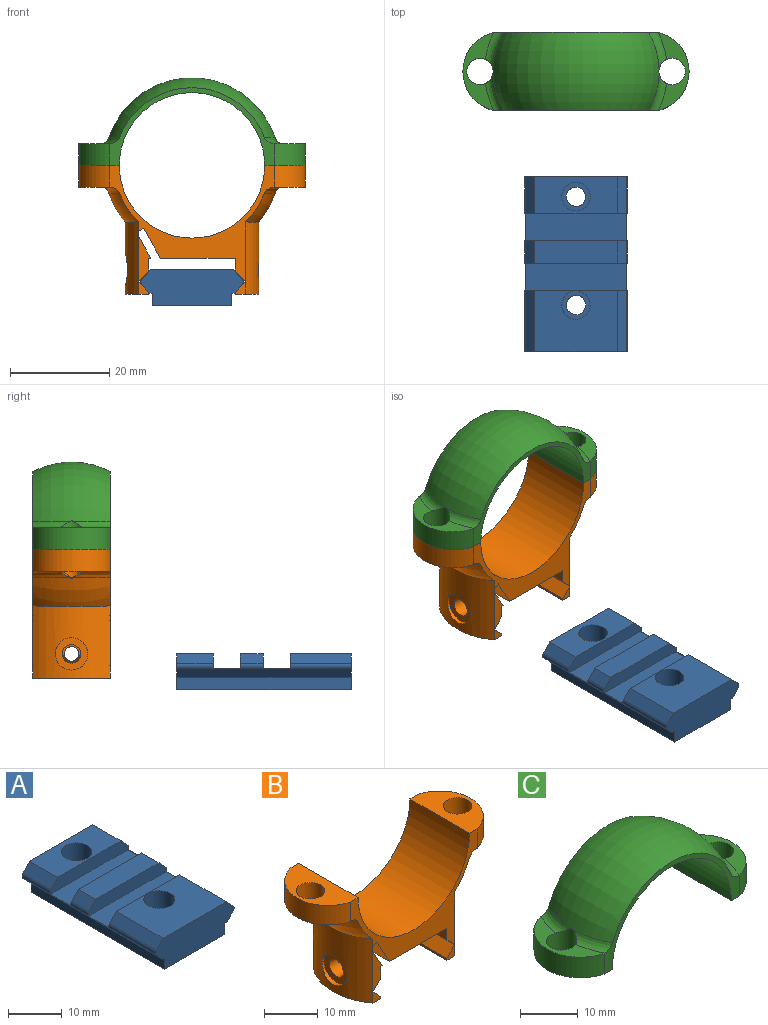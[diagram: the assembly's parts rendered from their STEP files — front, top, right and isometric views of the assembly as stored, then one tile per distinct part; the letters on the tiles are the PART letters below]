
ASSEMBLY  parts=3 mates=2
PART A: 32 faces, bbox 20.7x35.1x7.3 mm
  f0: cylinder r=0.75mm len=35.14mm, axis (0,1,0), area 28.3mm2, adj f1,f2,f14,f15,f18,f19,f20,f21
  f1: plane 4.57x1.92mm, normal (0.73,0,0.69), area 12.1mm2, adj f0,f3,f22,f24
  f2: plane 7.4x1.92mm, normal (0.73,0,0.69), area 19.6mm2, adj f0,f4,f19,f25
  f3: plane 16.66x4.57mm, normal (0,0,1), area 76.1mm2, adj f1,f5,f22,f24
  f4: plane 16.66x7.4mm, normal (0,0,1), area 97.3mm2, adj f2,f6,f19,f25,f31
  f5: plane 4.57x1.92mm, normal (-0.73,0,0.69), area 12.1mm2, adj f3,f7,f22,f24
  f6: plane 7.4x1.92mm, normal (-0.73,0,0.69), area 19.6mm2, adj f4,f7,f19,f25
  f7: cylinder r=0.75mm len=35.14mm, axis (0,1,0), area 28.3mm2, adj f5,f6,f8,f17,f18,f19,f20,f21
  f8: plane 35.14x1.8mm, normal (-0.73,0,-0.69), area 87mm2, adj f7,f9,f18,f19
  f9: plane 35.14x0.49mm, normal (0,0,-1), area 17.3mm2, adj f8,f10,f18,f19
  f10: plane 35.14x2.5mm, normal (-1,0,0), area 87.9mm2, adj f9,f11,f18,f19
  f11: plane 35.14x15.91mm, normal (0,0,-1), area 535.4mm2, adj f10,f12,f18,f19,f26,f29
  f12: plane 35.14x2.5mm, normal (1,0,0), area 87.9mm2, adj f11,f13,f18,f19
  f13: plane 35.14x0.49mm, normal (0,0,-1), area 17.3mm2, adj f12,f14,f18,f19
  f14: plane 35.14x1.8mm, normal (0.73,0,-0.69), area 87mm2, adj f0,f13,f18,f19
  f15: plane 12.29x1.92mm, normal (0.73,0,0.69), area 32.5mm2, adj f0,f16,f18,f21
  f16: plane 16.66x12.29mm, normal (0,0,1), area 178.8mm2, adj f15,f17,f18,f21,f28
  f17: plane 12.29x1.92mm, normal (-0.73,0,0.69), area 32.5mm2, adj f7,f16,f18,f21
  f18: plane 20.7x7.25mm, normal (0,-1,0), area 129.9mm2, adj f0,f7,f8,f9,f10,f11,f12,f13
  f19: plane 20.7x7.25mm, normal (0,1,0), area 129.9mm2, adj f0,f2,f4,f6,f7,f8,f9,f10
  f20: plane 20.38x5.44mm, normal (0,0,1), area 110.9mm2, adj f0,f7,f21,f22
  f21: plane 20.7x2.9mm, normal (0,1,0), area 55.6mm2, adj f0,f7,f15,f16,f17,f20
  f22: plane 20.7x2.9mm, normal (0,-1,0), area 55.6mm2, adj f0,f1,f3,f5,f7,f20
  f23: plane 20.38x5.44mm, normal (0,0,1), area 110.9mm2, adj f0,f7,f24,f25
  f24: plane 20.7x2.9mm, normal (0,1,0), area 55.6mm2, adj f0,f1,f3,f5,f7,f23
  f25: plane 20.7x2.9mm, normal (0,-1,0), area 55.6mm2, adj f0,f2,f4,f6,f7,f23
  f26: cylinder r=1.94mm len=3.88mm, axis (0,0,1), area 37.2mm2, adj f11,f27
  f27: plane 5.75x5.75mm, normal (0,0,1), area 14.1mm2, adj f26,f28
  f28: cylinder r=2.88mm len=5.75mm, axis (0,0,1), area 75.9mm2, adj f16,f27
  f29: cylinder r=1.94mm len=3.88mm, axis (0,0,1), area 37.2mm2, adj f11,f30
  f30: plane 5.75x5.75mm, normal (0,0,1), area 14.1mm2, adj f29,f31
  f31: cylinder r=2.88mm len=5.75mm, axis (0,0,1), area 75.9mm2, adj f4,f30
PART B: 53 faces, bbox 46.4x20.6x26.1 mm
  f0: cylinder r=12.78mm len=15.65mm, axis (0,0,-1), area 238.4mm2, adj f3,f5,f7,f11,f22,f29,f44
  f1: cylinder r=12.78mm len=15.65mm, axis (0,0,-1), area 211.7mm2, adj f2,f3,f5,f6,f8,f9,f12,f30
  f2: plane 9.08x2.44mm, normal (0,-1,0), area 12.6mm2, adj f1,f15,f16,f17,f37
  f3: plane 33.42x23.55mm, normal (0,1,0), area 144.3mm2, adj f0,f1,f4,f10,f18,f19,f24,f25
  f4: plane 15.65x15.08mm, normal (0,0,-1), area 235.9mm2, adj f3,f5,f18,f38
  f5: plane 33.42x23.55mm, normal (0,-1,0), area 144.3mm2, adj f0,f1,f4,f10,f18,f19,f24,f25
  f6: plane 2.55x2mm, normal (0,-1,0), area 3mm2, adj f1,f12,f13,f14
  f7: plane 2.55x2mm, normal (0,1,0), area 3mm2, adj f0,f20,f21,f22
  f8: plane 9.08x2.44mm, normal (0,1,0), area 12.6mm2, adj f1,f15,f16,f17,f37
  f9: plane 2.55x2mm, normal (0,1,0), area 3mm2, adj f1,f12,f13,f14
  f10: cylinder r=14.62mm len=29.25mm, axis (0,1,0), area 719.1mm2, adj f3,f5,f26,f32
  f11: plane 2.55x2mm, normal (0,-1,0), area 3mm2, adj f0,f20,f21,f22
  f12: plane 15.65x4.68mm, normal (0,0,-1), area 59.9mm2, adj f1,f6,f9,f13
  f13: plane 15.65x0.43mm, normal (1,0,0), area 6.7mm2, adj f6,f9,f12,f14
  f14: plane 15.65x2.12mm, normal (0.73,0,0.69), area 45.6mm2, adj f6,f9,f13,f15
  f15: plane 15.65x2.12mm, normal (0.73,0,-0.69), area 39.4mm2, adj f2,f8,f14,f16,f41
  f16: plane 15.65x2.59mm, normal (1,0,0), area 34.2mm2, adj f2,f8,f15,f17,f41
  f17: plane 15.65x0.44mm, normal (0,0,-1), area 6.9mm2, adj f2,f8,f16,f37
  f18: plane 15.65x2.59mm, normal (-1,0,0), area 36.4mm2, adj f3,f4,f5,f19,f44
  f19: plane 15.65x2.12mm, normal (-0.73,0,-0.69), area 41.9mm2, adj f3,f5,f18,f20,f44
  f20: plane 15.65x2.12mm, normal (-0.73,0,0.69), area 45.6mm2, adj f7,f11,f19,f21
  f21: plane 15.65x0.43mm, normal (-1,0,0), area 6.7mm2, adj f7,f11,f20,f22
  f22: plane 15.65x4.68mm, normal (0,0,-1), area 59.9mm2, adj f0,f7,f11,f21
  f23: cylinder r=2.65mm len=5.47mm, axis (0,0,-1), area 70.6mm2, adj f26,f45,f46,f47,f48
  f24: cylinder r=8.06mm len=15.65mm, axis (0,0,1), area 94.2mm2, adj f3,f5,f25,f26
  f25: plane 15.66x6.23mm, normal (0,0,-1), area 31.1mm2, adj f3,f5,f24,f27,f28,f48
  f26: plane 15.65x8.13mm, normal (0,0,1), area 80.4mm2, adj f3,f5,f10,f23,f24
  f27: bspline ~10.49x4.43mm, area 14.4mm2, adj f3,f25,f29,f46
  f28: bspline ~10.39x4.73mm, area 14.4mm2, adj f5,f25,f29,f47
  f29: torus R=1.32mm, axis (0,1,0), area 109.2mm2, adj f0,f3,f5,f27,f28,f45
  f30: torus R=1.32mm, axis (0,1,0), area 109.2mm2, adj f1,f3,f5,f31,f35,f51
  f31: bspline ~10.49x4.43mm, area 14.4mm2, adj f5,f30,f33,f49
  f32: plane 15.65x8.13mm, normal (0,0,1), area 80.4mm2, adj f3,f5,f10,f34,f36
  f33: plane 15.66x6.23mm, normal (0,0,-1), area 31.1mm2, adj f3,f5,f31,f34,f35,f50
  f34: cylinder r=8.06mm len=15.65mm, axis (0,0,1), area 94.2mm2, adj f3,f5,f32,f33
  f35: bspline ~10.39x4.73mm, area 14.4mm2, adj f3,f30,f33,f52
  f36: cylinder r=2.65mm len=5.64mm, axis (0,0,-1), area 69.6mm2, adj f32,f49,f50,f51,f52
  f37: plane 15.65x4.38mm, normal (0.87,0,0.49), area 78.4mm2, adj f2,f8,f17,f40
  f38: plane 15.65x6mm, normal (-0.87,0,-0.49), area 107.5mm2, adj f3,f4,f5,f39
  f39: plane 15.65x1.02mm, normal (0.49,0,-0.87), area 18.2mm2, adj f3,f5,f38,f40
  f40: plane 15.65x1.06mm, normal (1,0,0), area 16.5mm2, adj f1,f37,f39
  f41: cylinder r=1.86mm len=3.81mm, axis (-1,0,0), area 39.3mm2, adj f15,f16,f42
  f42: plane 6.5x6.5mm, normal (-1,0,0), area 22.3mm2, adj f41,f43
  f43: cylinder r=3.25mm len=6.5mm, axis (-1,0,0), area 17.8mm2, adj f1,f42
  f44: cylinder r=1.46mm len=4.68mm, axis (-1,0,0), area 40mm2, adj f0,f18,f19
  f45: bspline ~1.86x0.64mm, area 0.2mm2, adj f23,f29,f46,f47
  f46: bspline ~2.72x2.01mm, area 1.6mm2, adj f23,f27,f45,f48
  f47: bspline ~2.74x2.02mm, area 1.6mm2, adj f23,f28,f45,f48
  f48: torus R=3.15mm, axis (0,0,-1), area 8.7mm2, adj f23,f25,f46,f47
  f49: bspline ~2.72x2.01mm, area 1.6mm2, adj f31,f36,f50,f51
  f50: torus R=3.15mm, axis (0,0,-1), area 8.7mm2, adj f33,f36,f49,f52
  f51: bspline ~1.86x0.64mm, area 0.2mm2, adj f30,f36,f49,f52
  f52: bspline ~2.74x2.02mm, area 1.6mm2, adj f35,f36,f50,f51
PART C: 16 faces, bbox 45.7x20.6x15.8 mm
  f0: torus R=1.32mm, axis (0,1,0), area 678.2mm2, adj f1,f2,f3,f4,f5,f13,f14,f15
  f1: bspline ~10.49x4.43mm, area 15.2mm2, adj f0,f4,f10,f15
  f2: bspline ~10.39x4.73mm, area 15.2mm2, adj f0,f4,f9,f14
  f3: bspline ~10.49x4.43mm, area 15.2mm2, adj f0,f5,f9,f14
  f4: plane 33.42x15.79mm, normal (0,-1,0), area 58.9mm2, adj f0,f1,f2,f6,f7,f8,f9,f10
  f5: plane 33.42x15.79mm, normal (0,1,0), area 58.9mm2, adj f0,f3,f6,f7,f8,f9,f10,f11
  f6: plane 15.65x8.13mm, normal (0,0,-1), area 80.4mm2, adj f4,f5,f7,f11,f15
  f7: cylinder r=14.62mm len=29.25mm, axis (0,1,0), area 719.1mm2, adj f4,f5,f6,f8
  f8: plane 15.65x8.13mm, normal (0,0,-1), area 80.4mm2, adj f4,f5,f7,f12,f14
  f9: plane 15.66x6.23mm, normal (0,0,1), area 36.8mm2, adj f2,f3,f4,f5,f12,f14
  f10: plane 15.66x6.23mm, normal (0,0,1), area 36.8mm2, adj f1,f4,f5,f11,f13,f15
  f11: cylinder r=8.06mm len=15.65mm, axis (0,0,-1), area 94.2mm2, adj f4,f5,f6,f10
  f12: cylinder r=8.06mm len=15.65mm, axis (0,0,-1), area 94.2mm2, adj f4,f5,f8,f9
  f13: bspline ~10.39x4.73mm, area 15.2mm2, adj f0,f5,f10,f15
  f14: cylinder r=2.65mm len=5.63mm, axis (0,0,1), area 77.5mm2, adj f0,f2,f3,f8,f9
  f15: cylinder r=2.65mm len=5.72mm, axis (0,0,1), area 76.8mm2, adj f0,f1,f6,f10,f13
PLACE A t=(0.25,-3.46,32.58)mm
PLACE B t=(0.25,17.66,32.64)mm
PLACE C t=(0.25,17.66,32.64)mm fixed
MATE fastened B.f32 <-> C.f6  axis (0,0,1) through (-14.37,17.66,32.64)mm
MATE slider A.f19 <-> B.f3  axis (0,1,0) through (0.25,-3.46,8.14)mm
